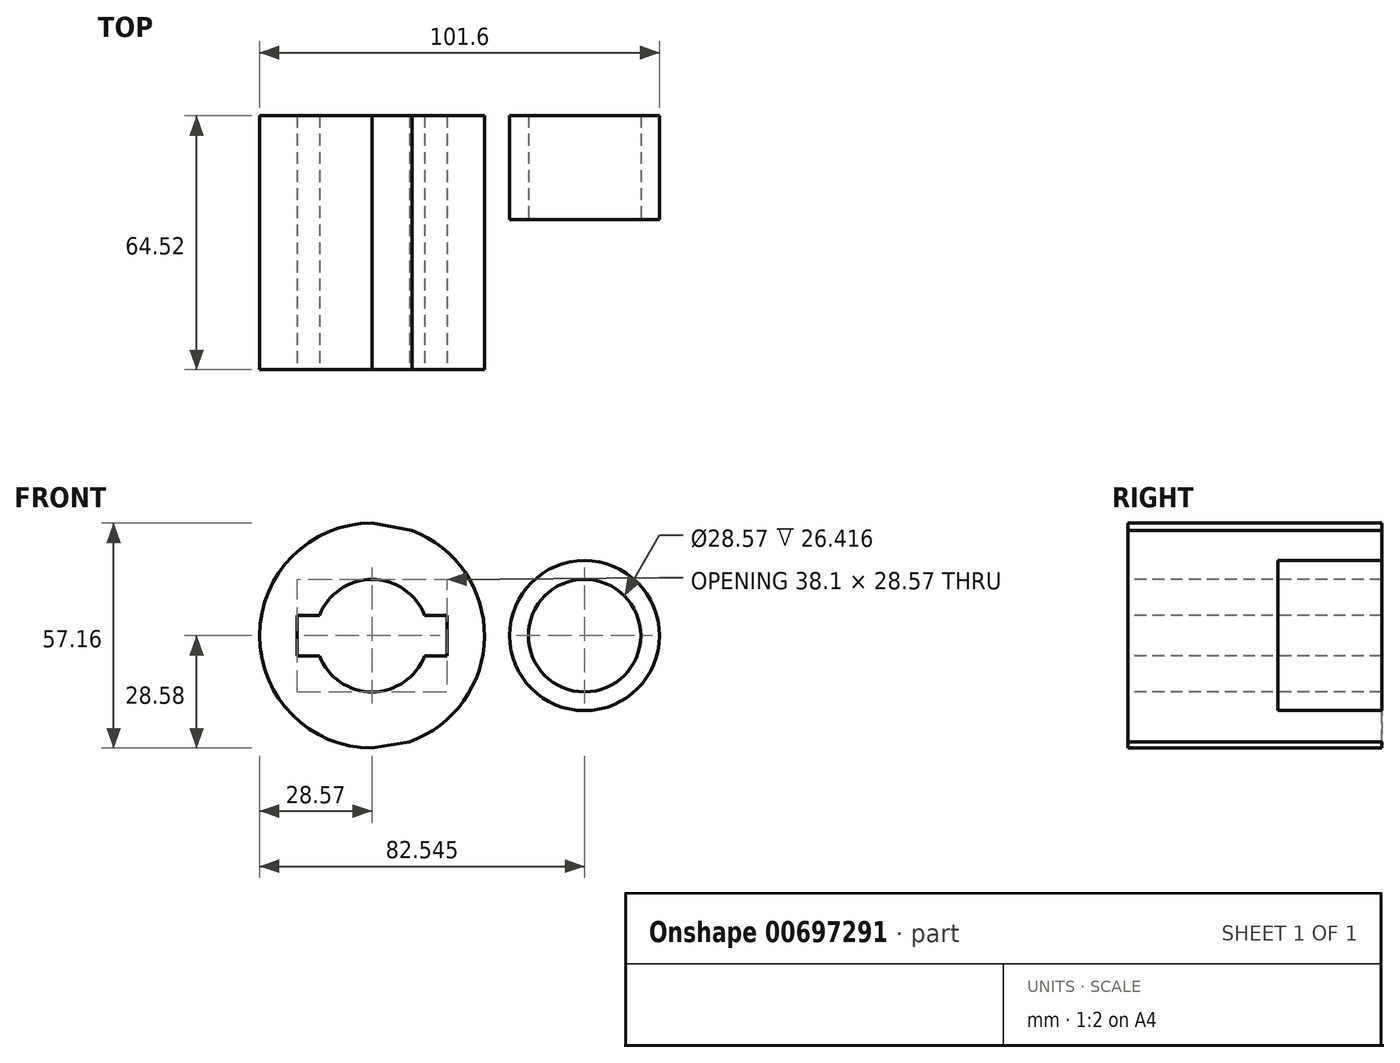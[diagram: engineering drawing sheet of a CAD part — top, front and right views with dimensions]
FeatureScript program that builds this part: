
annotation { "Feature Type Name" : "Feature", "Feature Type Description" : "" }
export const myFeature = defineFeature(function(context is Context, id is Id, definition is map)
    precondition{}
    {
        {
            var Q0;
            Q0=qCreatedBy(makeId("Front.planeOp"),FACE);
            var sketch = newSketch(context, id + "F0", { "sketchPlane" : qUnion([Q0])});
            skCircle(sketch, "E0", {"center": v(0, 0) * mm, "radius": 28.58 * mm});
            skCircle(sketch, "E1", {"center": v(53.98, 0) * mm, "radius": 19.05 * mm});
            skLineSegment(sketch, "E2", {"start": v(0, 28.57) * mm, "end": v(52.44, 18.99) * mm});
            skLineSegment(sketch, "E3", {"start": v(0, -28.58) * mm, "end": v(57.2, -18.78) * mm});
            skCircle(sketch, "E4", {"center": v(0, 0) * mm, "radius": 14.29 * mm});
            skCircle(sketch, "E5", {"center": v(53.98, 0) * mm, "radius": 14.29 * mm});
            skLineSegment(sketch, "E6.bottom", {"start": v(19.05, -5.13) * mm, "end": v(-19.05, -5.13) * mm});
            skLineSegment(sketch, "E6.top", {"start": v(19.05, 5.13) * mm, "end": v(-19.05, 5.13) * mm});
            skLineSegment(sketch, "E6.left", {"start": v(19.05, -5.13) * mm, "end": v(19.05, 5.13) * mm});
            skLineSegment(sketch, "E6.right", {"start": v(-19.05, -5.13) * mm, "end": v(-19.05, 5.13) * mm});
            skSolve(sketch);
        }
        {
            var Q0;
            {var subQ0=sQuery(id+"F0.wireOp",EDGE,"E2");var subQ1=sQuery(id+"F0.wireOp",EDGE,"E0");var subQ2=makeQuery(id+"F0.imprint","INTERSECT",VERTEX,{"disambiguationData":[OD(1.0)],"derivedFrom":[subQ1,subQ0]});Q0=makeQuery(id+"F0.imprint","IMPRINT",FACE,{"disambiguationData":[TD([[makeQuery(id+"F0.imprint","IMPRINT",EDGE,{"disambiguationData":[TD([[subQ2,1.0]])],"derivedFrom":subQ1}),-1.0]])]});}
            var Q1;
            Q1=makeQuery(id+"F0.imprint","IMPRINT",FACE,{"disambiguationData":[TD([[makeQuery(id+"F0.imprint","IMPRINT",EDGE,{"derivedFrom":sQuery(id+"F0.wireOp",EDGE,"E5")}),-1.0]])]});
            var Q2;
            {var subQ0=sQuery(id+"F0.wireOp",EDGE,"E2");var subQ1=sQuery(id+"F0.wireOp",EDGE,"E0");var subQ2=makeQuery(id+"F0.imprint","INTERSECT",VERTEX,{"disambiguationData":[OD(0.0)],"derivedFrom":[subQ1,subQ0]});Q2=makeQuery(id+"F0.imprint","IMPRINT",FACE,{"disambiguationData":[TD([[makeQuery(id+"F0.imprint","IMPRINT",EDGE,{"disambiguationData":[TD([[subQ2,1.0]])],"derivedFrom":subQ1}),1.0]])]});}
            var Q3;
            {var subQ0=sQuery(id+"F0.wireOp",EDGE,"E3");var subQ1=sQuery(id+"F0.wireOp",EDGE,"E0");var subQ2=makeQuery(id+"F0.imprint","INTERSECT",VERTEX,{"disambiguationData":[OD(0.0)],"derivedFrom":[subQ1,subQ0]});Q3=makeQuery(id+"F0.imprint","IMPRINT",FACE,{"disambiguationData":[TD([[makeQuery(id+"F0.imprint","IMPRINT",EDGE,{"disambiguationData":[TD([[subQ2,-1.0]])],"derivedFrom":subQ1}),1.0]])]});}
            var Q4;
            {var subQ4=sQuery(id+"F0.wireOp",EDGE,"E6.left");Q4=makeQuery(id+"F0.imprint","IMPRINT",FACE,{"disambiguationData":[TD([[makeQuery(id+"F0.imprint","IMPRINT",EDGE,{"derivedFrom":subQ4}),-1.0]])]});}
            extrude(context, id + "F1", {"entities" : qUnion([Q0, Q1, Q2, Q3, Q4]), "oppositeDirection" : true, "depth" : 26.42 * mm, "offsetDistance" : 25.4 * mm});
        }
        {
            var Q0;
            {var subQ4=sQuery(id+"F0.wireOp",EDGE,"E6.left");Q0=makeQuery(id+"F0.imprint","IMPRINT",FACE,{"disambiguationData":[TD([[makeQuery(id+"F0.imprint","IMPRINT",EDGE,{"derivedFrom":subQ4}),-1.0]])]});}
            extrude(context, id + "F2", {"entities" : qUnion([Q0]), "operationType" : NewBodyOperationType.ADD, "depth" : 38.1 * mm, "offsetDistance" : 25.4 * mm});
        }
    });
